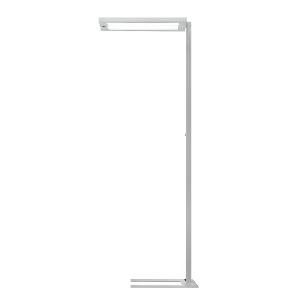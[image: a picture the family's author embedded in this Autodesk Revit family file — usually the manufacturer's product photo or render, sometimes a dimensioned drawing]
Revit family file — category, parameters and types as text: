
# Revit family: lavigo_core_-_dps_9000_840_r_g1_ws_00812470_4f97
name_source: partatom
category: Lighting Fixtures
units: mm (PartAtom-declared; Revit-internal decimal feet)

## family parameters
Cut with Voids When Loaded = No
Host = Face
Light Source = No
Part Type = Normal
Room Calculation Point = No
Round Connector Dimension = Use Diameter
Shared = No

## types (1)
- LAVIGO.core - DPS 9000/840/R/G1/WS (1 x LED, 8900 lm, 4000K)
    Apparent Load = 62 VA
    Approval mark = CE
    CIE Flux Codes = 59 88 97 35 100
    Color Rendering = 80-89
    Color Temperature = 4000K
    Control Gear = Electronic ballast
    Default Elevation = 1800 mm
    Description = DPS 9000/840/R/G1|Free-standing luminaire|light source: LED Cold white   |work equipment: Electronic ballast DALI|connected load: 220-240 V, 50/60 Hz|Power consumption: approx. 62 W|standby: approx. 0,30|power factor: approx. 0,959|luminous flux: 8900 lm|luminous efficacy: 143 lm/W|light distribution: Direct/indirect|direct ratio: approx. 35 %|color rendering index (CRI): >= 80|chromaticity tolerance:  3 SDCM|technology: Presence and daylight sensor control (PIR)|operation: Rocker switch|luminaire body|material: Steel/plastic|surface: Painted|colour: White|lamp cover: Polycarbonate (PC), Clear|tubular section|material: Steel tube|surface: Painted|Form: Tubular section upright|colour of tubular section: White|luminaire base|Form: C-form flat|weight (net): approx. 14.7 kg|mains lead: 3.00 m Mains plug CEE 7/VII|Fastening: Floor standing base|decorative contrast side parts: Flint grey|glare control: Prism aperture|luminance(L65): <= 4400 cd/m|unified glare rating(4H 8H): <=  16|special features: Luminaire head detachable, Direct and indirect light switchable together, Flicker-free, Integrated light and presence sensor PIR, Motion sensor time-out of 15mins~|Approval mark: US~B_0014~VDE - ENEC|
    Frequency = 50 Hz, 60 Hz
    Height = 36 mm
    Lamp = 1 x LED
    Lamp Light Flux = 8900 lm
    Lamp count = 1
    Length = 675 mm
    Luminous efficacy = 144 lm/W
    Manufacturer = Waldmann
    ModVariant = No
    Model = 00812470
    Mounting Place = Floor
    Mounting Type = Freestanding
    Number of Poles = 1
    OnlyDefault = Yes
    Power Factor = 1
    Product Name = LAVIGO.core - DPS 9000/840/R/G1/WS
    Product group = Free standing luminaire
    ProductGroupID = 13
    Protection Class = Protection class I
    Protection Degree = IP 20
    RLX_Detail_Level = 1
    RLX_Emergency_Light_Flux = 0 lm
    RLX_Emergency_Type = 0
    RLX_Emergency_Type_DB = No
    RlxData = <blob elided: 32625 chars, md5=9bb62290>
    Socket = socket
    Standby Power = 0 W
    System Light Flux = 8900 lm
    System Power = 62 W
    Type Comments = Product without accessories
    Type Image = 121805000-00747395.jpg
    URL = http://relux.com
    VarID = ---
    Voltage = 230 V
    Voltage Range = 220-240 V
    Weight = 0.00 kg
    Width = 320 mm

## geometry (parser evidence)
native form markers: Blend x4, Sweep x16
no freeform markers — native parametric forms only
